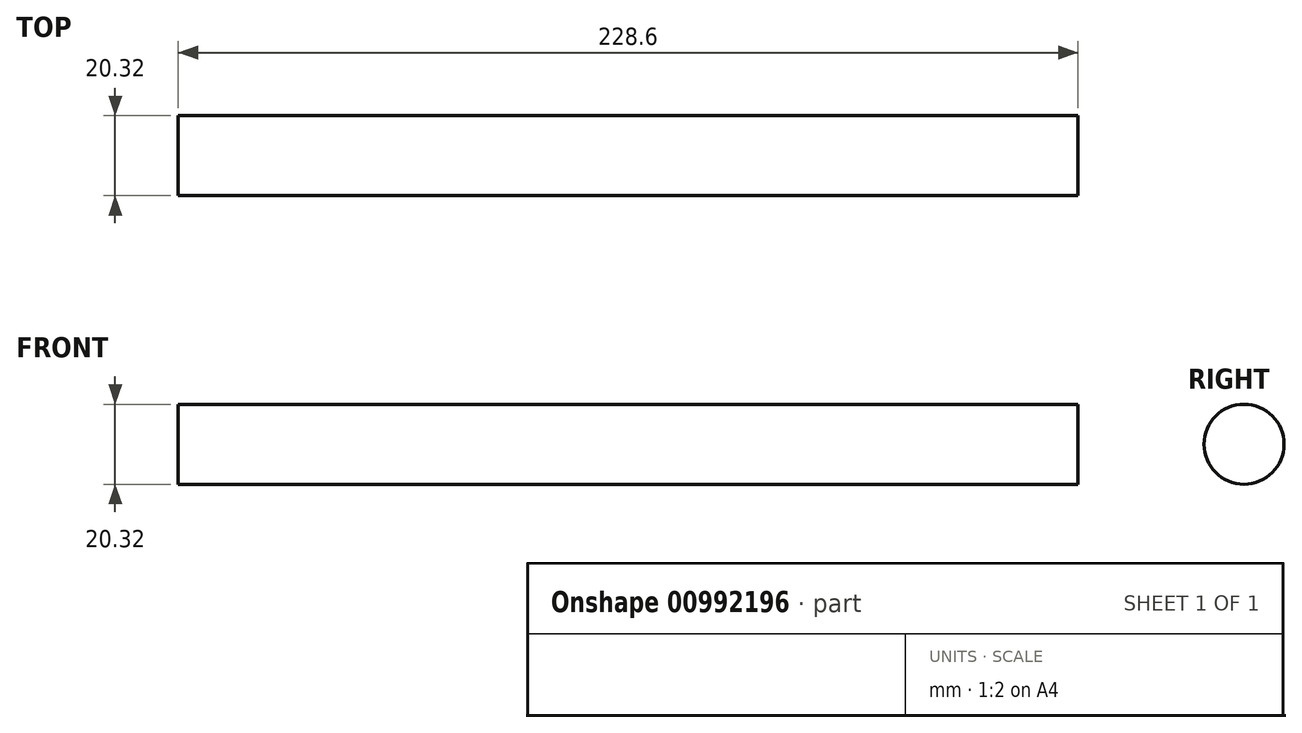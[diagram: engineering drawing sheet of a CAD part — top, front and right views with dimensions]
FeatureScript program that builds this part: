
annotation { "Feature Type Name" : "Feature", "Feature Type Description" : "" }
export const myFeature = defineFeature(function(context is Context, id is Id, definition is map)
    precondition{}
    {
        {
            var Q0;
            Q0=qCreatedBy(makeId("Right.planeOp"),FACE);
            var sketch = newSketch(context, id + "F0", { "sketchPlane" : qUnion([Q0])});
            skCircle(sketch, "E0", {"center": v(0, 0) * mm, "radius": 10.16 * mm});
            skSolve(sketch);
        }
        {
            var Q0;
            Q0 = qSketchRegion(id + "F0", true);
            extrude(context, id + "F1", {"entities" : qUnion([Q0]), "depth" : 228.6 * mm, "offsetDistance" : 25.4 * mm});
        }
    });
